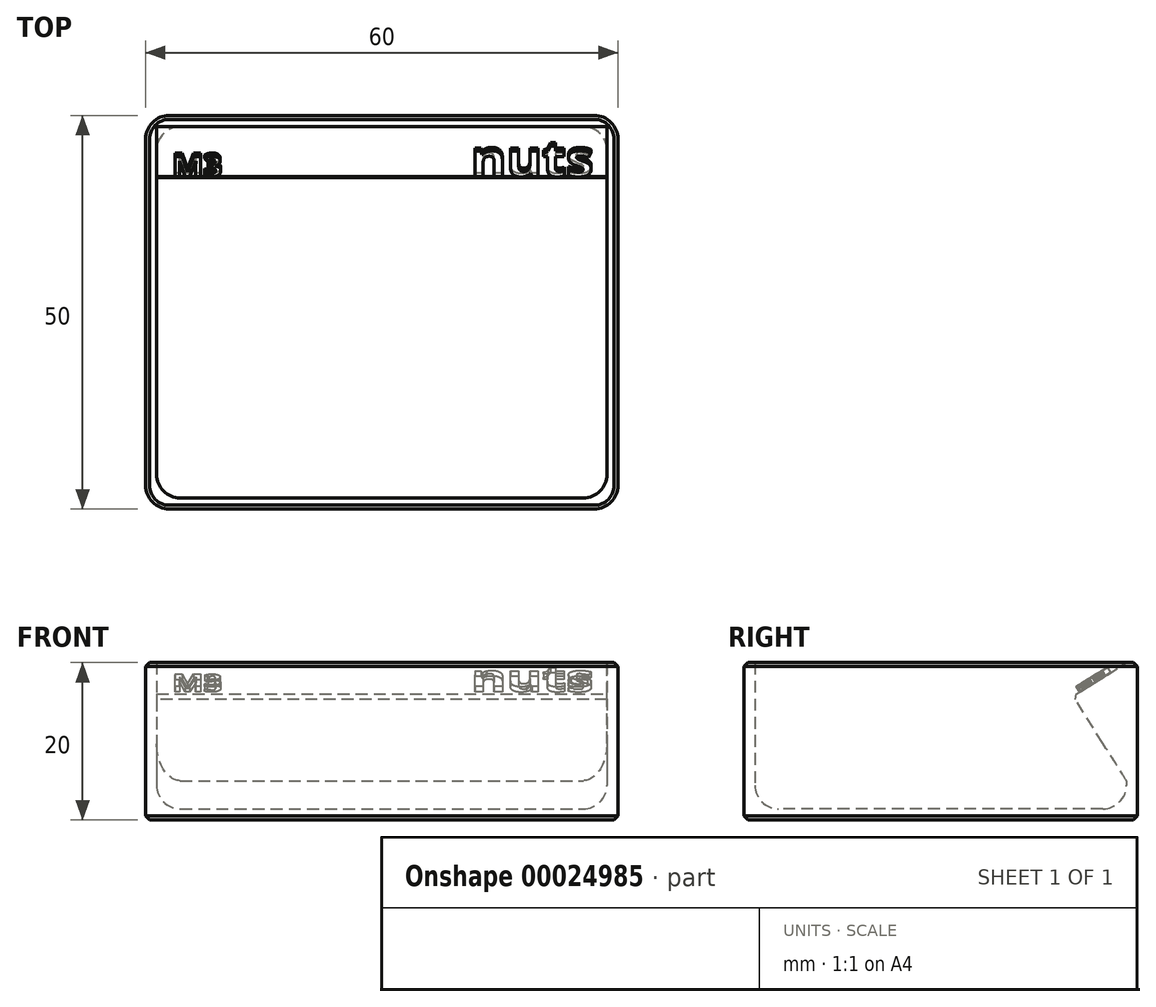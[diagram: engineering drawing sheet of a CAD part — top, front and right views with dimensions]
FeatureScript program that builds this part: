
annotation { "Feature Type Name" : "Feature", "Feature Type Description" : "" }
export const myFeature = defineFeature(function(context is Context, id is Id, definition is map)
    precondition{}
    {
        {
            var Q0;
            Q0=qCreatedBy(makeId("Top.planeOp"),FACE);
            var sketch = newSketch(context, id + "F0", { "sketchPlane" : qUnion([Q0])});
            skLineSegment(sketch, "E0.rect.bottom", {"start": v(-30, 25) * mm, "end": v(30, 25) * mm});
            skLineSegment(sketch, "E0.rect.top", {"start": v(-30, -25) * mm, "end": v(30, -25) * mm});
            skLineSegment(sketch, "E0.rect.left", {"start": v(-30, 25) * mm, "end": v(-30, -25) * mm});
            skLineSegment(sketch, "E0.rect.right", {"start": v(30, 25) * mm, "end": v(30, -25) * mm});
            skPoint(sketch, "E0.rect.middle", {"position": v(0, 0) * mm});
            skSolve(sketch);
        }
        {
            var Q0;
            Q0=makeQuery(id+"F0.imprint","IMPRINT",FACE,{"disambiguationData":[TD([[makeQuery(id+"F0.imprint","IMPRINT",EDGE,{"derivedFrom":sQuery(id+"F0.wireOp",EDGE,"E0.rect.bottom")}),-1.0]])]});
            extrude(context, id + "F1", {"entities" : qUnion([Q0]), "depth" : 20 * mm});
        }
        {
            var Q0;
            Q0=makeQuery(id+"F1.opExtrude","CAP_FACE",FACE,{"disambiguationData":[OSD([sQuery(id+"F0.wireOp",EDGE,"E0.rect.bottom"),sQuery(id+"F0.wireOp",EDGE,"E0.rect.top"),sQuery(id+"F0.wireOp",EDGE,"E0.rect.left"),sQuery(id+"F0.wireOp",EDGE,"E0.rect.right")])],"isStart":false});
            shell(context, id + "F2", {"entities" : qUnion([Q0]), "thickness" : 1.4 * mm});
        }
        {
            var Q0;
            Q0=makeQuery(id+"F2.opShell","OFFSET_FACE",FACE,{"disambiguationData":[OSD([sQuery(id+"F0.wireOp",EDGE,"E0.rect.right")])]});
            var sketch = newSketch(context, id + "F3", { "sketchPlane" : qUnion([Q0])});
            skLineSegment(sketch, "E1", {"start": v(-23.6, 20) * mm, "end": v(-23.6, 5) * mm});
            skLineSegment(sketch, "E2", {"start": v(-23.6, 5) * mm, "end": v(-14.14, 20) * mm});
            skLineSegment(sketch, "E3", {"start": v(-16.83, 15.73) * mm, "end": v(-23.6, 20) * mm});
            skSolve(sketch);
        }
        {
            var Q0;
            Q0=makeQuery(id+"F3.imprint","IMPRINT",FACE,{"disambiguationData":[TD([[makeQuery(id+"F3.imprint","IMPRINT",EDGE,{"derivedFrom":sQuery(id+"F3.wireOp",EDGE,"E1")}),1.0]])]});
            extrude(context, id + "F4", {"entities" : qUnion([Q0]), "operationType" : NewBodyOperationType.ADD, "endBound" : BoundingType.UP_TO_NEXT, "depth" : 15 * mm});
        }
        {
            var Q0;
            Q0=makeQuery(id+"F4.opExtrude","SWEPT_FACE",FACE,{"disambiguationData":[OSD([sQuery(id+"F3.wireOp",EDGE,"E3")])]});
            var sketch = newSketch(context, id + "F5", { "sketchPlane" : qUnion([Q0])});
            skText(sketch, "E4", { "text": "nuts", "fontName": "OpenSans-Bold.ttf"});
            skText(sketch, "E5", { "text": "M3", "fontName": "OpenSans-Bold.ttf"});
            const initialGuessF5  = {"E4": [0.01127, 0.02363, 1, 0, 0.005], "E5": [-0.0266, 0.02363, 1, 0, 0.003]};
            skSetInitialGuess(sketch, initialGuessF5);
            skSolve(sketch);
        }
        {
            var Q0;
            Q0 = qSketchRegion(id + "F5", true);
            extrude(context, id + "F6", {"entities" : qUnion([Q0]), "operationType" : NewBodyOperationType.ADD, "depth" : .8 * mm});
        }
        {
            var Q0;
            Q0=makeQuery(id+"F1.opExtrude","SWEPT_EDGE",EDGE,{"disambiguationData":[OSD([sQuery(id+"F0.wireOp",EDGE,"E0.rect.top"),sQuery(id+"F0.wireOp",EDGE,"E0.rect.right")])]});
            var Q1;
            Q1=makeQuery(id+"F2.opShell","OFFSET_EDGE",EDGE,{"disambiguationData":[OSD([sQuery(id+"F0.wireOp",EDGE,"E0.rect.top"),sQuery(id+"F0.wireOp",EDGE,"E0.rect.right")])]});
            var Q2;
            Q2=makeQuery(id+"F2.opShell","OFFSET_EDGE",EDGE,{"disambiguationData":[OSD([sQuery(id+"F0.wireOp",EDGE,"E0.rect.top"),sQuery(id+"F0.wireOp",EDGE,"E0.rect.left")])]});
            var Q3;
            Q3=makeQuery(id+"F1.opExtrude","SWEPT_EDGE",EDGE,{"disambiguationData":[OSD([sQuery(id+"F0.wireOp",EDGE,"E0.rect.top"),sQuery(id+"F0.wireOp",EDGE,"E0.rect.left")])]});
            var Q4;
            Q4=makeQuery(id+"F2.opShell","OFFSET_EDGE",EDGE,{"disambiguationData":[OSD([sQuery(id+"F0.wireOp",EDGE,"E0.rect.bottom"),sQuery(id+"F0.wireOp",EDGE,"E0.rect.right")])]});
            var Q5;
            Q5=makeQuery(id+"F1.opExtrude","SWEPT_EDGE",EDGE,{"disambiguationData":[OSD([sQuery(id+"F0.wireOp",EDGE,"E0.rect.bottom"),sQuery(id+"F0.wireOp",EDGE,"E0.rect.right")])]});
            var Q6;
            Q6=makeQuery(id+"F2.opShell","OFFSET_EDGE",EDGE,{"disambiguationData":[OSD([sQuery(id+"F0.wireOp",EDGE,"E0.rect.bottom"),sQuery(id+"F0.wireOp",EDGE,"E0.rect.left")])]});
            var Q7;
            Q7=makeQuery(id+"F1.opExtrude","SWEPT_EDGE",EDGE,{"disambiguationData":[OSD([sQuery(id+"F0.wireOp",EDGE,"E0.rect.bottom"),sQuery(id+"F0.wireOp",EDGE,"E0.rect.left")])]});
            var Q8;
            {var subQ0=sQuery(id+"F0.wireOp",EDGE,"E0.rect.bottom");Q8=makeQuery(id+"F2.opShell","OFFSET_EDGE",EDGE,{"disambiguationData":[OSD([subQ0]),TDD([makeQuery(id+"F1.opExtrude","CAP_EDGE",EDGE,{"disambiguationData":[OSD([subQ0])],"isStart":true})])]});}
            var Q9;
            {var subQ0=sQuery(id+"F0.wireOp",EDGE,"E0.rect.left");Q9=makeQuery(id+"F2.opShell","OFFSET_EDGE",EDGE,{"disambiguationData":[OSD([subQ0]),TDD([makeQuery(id+"F1.opExtrude","CAP_EDGE",EDGE,{"disambiguationData":[OSD([subQ0])],"isStart":true})])]});}
            var Q10;
            {var subQ0=sQuery(id+"F0.wireOp",EDGE,"E0.rect.top");Q10=makeQuery(id+"F2.opShell","OFFSET_EDGE",EDGE,{"disambiguationData":[OSD([subQ0]),TDD([makeQuery(id+"F1.opExtrude","CAP_EDGE",EDGE,{"disambiguationData":[OSD([subQ0])],"isStart":true})])]});}
            var Q11;
            {var subQ0=sQuery(id+"F0.wireOp",EDGE,"E0.rect.right");Q11=makeQuery(id+"F2.opShell","OFFSET_EDGE",EDGE,{"disambiguationData":[OSD([subQ0]),TDD([makeQuery(id+"F1.opExtrude","CAP_EDGE",EDGE,{"disambiguationData":[OSD([subQ0])],"isStart":true})])]});}
            fillet(context, id + "F7", {"entities" : qUnion([Q0, Q1, Q2, Q3, Q4, Q5, Q6, Q7, Q8, Q9, Q10, Q11]), "radius" : 3 * mm, "tangentPropagation" : true, "allowEdgeOverflow" : false});
        }
        {
            var Q0;
            Q0=makeQuery(id+"F1.opExtrude","CAP_EDGE",EDGE,{"disambiguationData":[OSD([sQuery(id+"F0.wireOp",EDGE,"E0.rect.bottom")])],"isStart":false});
            var Q1;
            Q1=makeQuery(id+"F1.opExtrude","CAP_EDGE",EDGE,{"disambiguationData":[OSD([sQuery(id+"F0.wireOp",EDGE,"E0.rect.top")])],"isStart":true});
            var Q2;
            {var subQ0=sQuery(id+"F0.wireOp",EDGE,"E0.rect.bottom");Q2=makeQuery(id+"F2.opShell","OFFSET_EDGE",EDGE,{"disambiguationData":[OSD([subQ0]),TDD([makeQuery(id+"F1.opExtrude","CAP_EDGE",EDGE,{"disambiguationData":[OSD([subQ0])],"isStart":true})])]});}
            var Q3;
            Q3=makeQuery(id+"F4.opExtrude","CAP_EDGE",EDGE,{"disambiguationData":[OSD([sQuery(id+"F3.wireOp",EDGE,"E3")])],"isStart":false});
            var Q4;
            Q4=makeQuery(id+"F4.opExtrude","SWEPT_EDGE",EDGE,{"disambiguationData":[OSD([sQuery(id+"F3.wireOp",EDGE,"E2"),sQuery(id+"F3.wireOp",EDGE,"E3")])]});
            var Q5;
            Q5=makeQuery(id+"F4.opExtrude","CAP_EDGE",EDGE,{"disambiguationData":[OSD([sQuery(id+"F3.wireOp",EDGE,"E2")])],"isStart":false});
            chamfer(context, id + "F8", {"entities" : qUnion([Q0, Q1, Q2, Q3, Q4, Q5]), "width" : .5 * mm, "tangentPropagation" : true});
        }
    });
